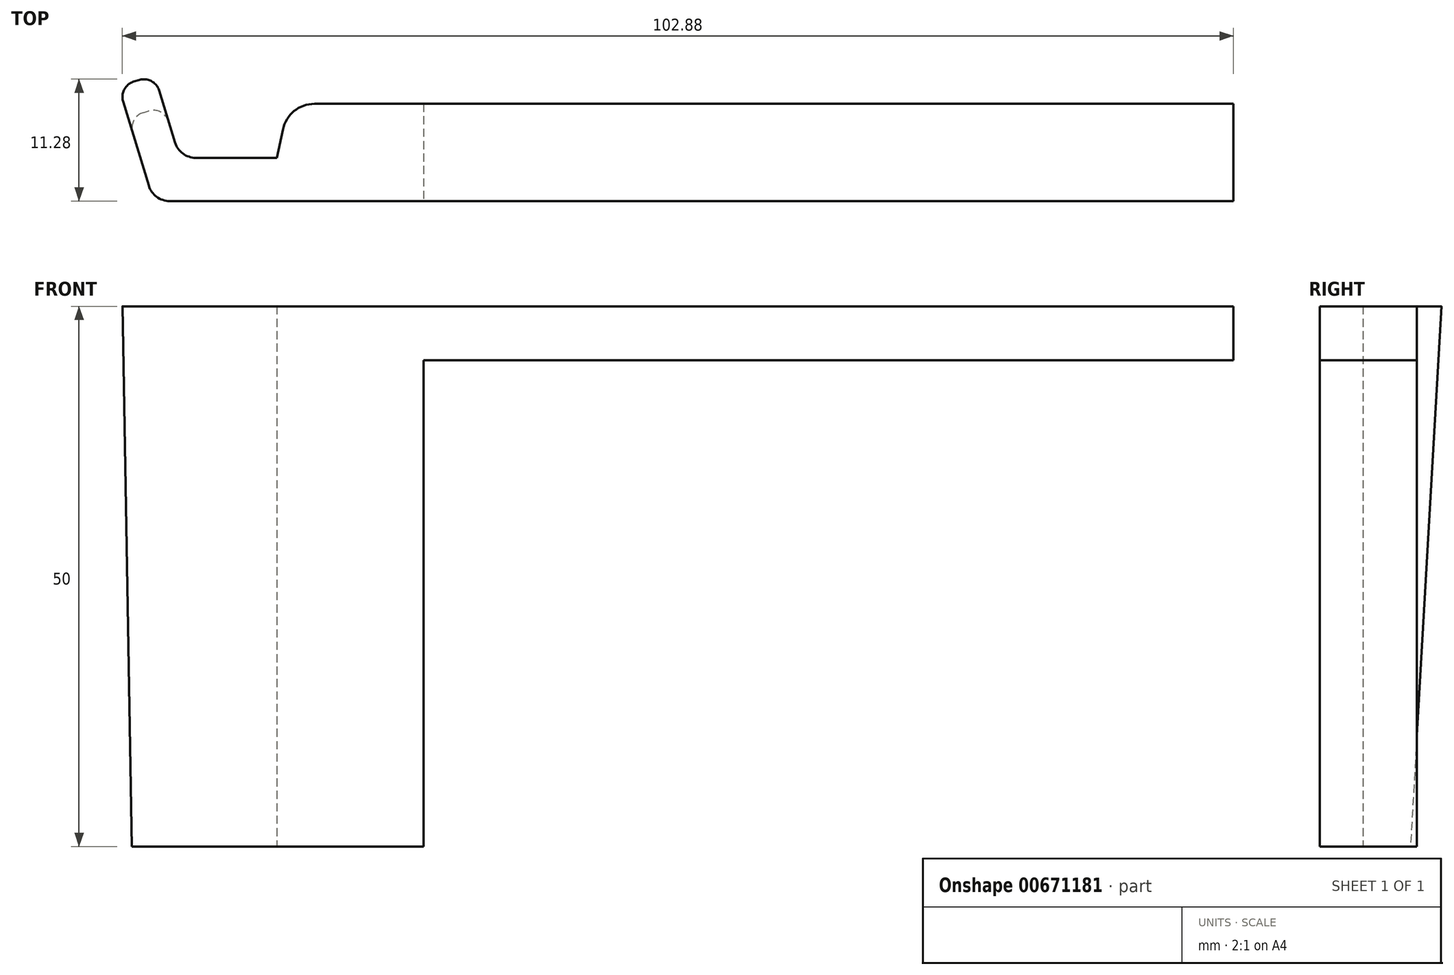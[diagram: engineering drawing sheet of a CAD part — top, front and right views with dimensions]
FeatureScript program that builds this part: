
annotation { "Feature Type Name" : "Feature", "Feature Type Description" : "" }
export const myFeature = defineFeature(function(context is Context, id is Id, definition is map)
    precondition{}
    {
        {
            var Q0;
            Q0=qCreatedBy(makeId("Top.planeOp"),FACE);
            var sketch = newSketch(context, id + "F0", { "sketchPlane" : qUnion([Q0])});
            skLineSegment(sketch, "E0", {"start": v(-7.72, 6.63) * mm, "end": v(-4.47, -4) * mm});
            skLineSegment(sketch, "E1", {"start": v(-4.47, -4) * mm, "end": v(20.53, -4) * mm});
            skLineSegment(sketch, "E2.0", {"start": v(-4.37, 7.65) * mm, "end": v(-2.03, 0) * mm});
            skLineSegment(sketch, "E3", {"start": v(-4.37, 7.65) * mm, "end": v(-7.72, 6.63) * mm});
            skLineSegment(sketch, "E4", {"start": v(6.97, 0) * mm, "end": v(-2.03, 0) * mm});
            skLineSegment(sketch, "E5", {"start": v(20.53, 5) * mm, "end": v(20.53, -4) * mm});
            skLineSegment(sketch, "E6", {"start": v(6.97, 0) * mm, "end": v(8, 5) * mm});
            skLineSegment(sketch, "E7", {"start": v(8, 5) * mm, "end": v(20.53, 5) * mm});
            skPoint(sketch, "E8.orphan", {"position": v(20.53, 0) * mm});
            skPoint(sketch, "E9.orphan", {"position": v(9.05, 10) * mm});
            skSolve(sketch);
        }
        {
            var Q0;
            Q0=qSketchRegion(id+"F0",true);
            extrude(context, id + "F1", {"entities" : qUnion([Q0]), "depth" : 50 * mm, "offsetDistance" : 25 * mm});
        }
        {
            var Q0;
            Q0=makeQuery(id+"F1.opExtrude","CAP_EDGE",EDGE,{"disambiguationData":[OSD([sQuery(id+"F0.wireOp",EDGE,"E3")])],"isStart":true});
            chamfer(context, id + "F2", {"entities" : qUnion([Q0]), "chamferType" : ChamferType.TWO_OFFSETS, "width1" : 50 * mm, "oppositeDirection" : false, "width2" : 3 * mm, "tangentPropagation" : true});
        }
        {
            var Q0;
            Q0=makeQuery(id+"F2.opChamfer","BLEND_EDGE",EDGE,{"blendedFrom":[makeQuery(id+"F1.opExtrude","CAP_EDGE",EDGE,{"disambiguationData":[OSD([sQuery(id+"F0.wireOp",EDGE,"E3")])],"isStart":true}),makeQuery(id+"F1.opExtrude","SWEPT_FACE",FACE,{"disambiguationData":[OSD([sQuery(id+"F0.wireOp",EDGE,"E2.0")])]})],"blendedInto":[makeQuery(id+"F1.opExtrude","SWEPT_FACE",FACE,{"disambiguationData":[OSD([sQuery(id+"F0.wireOp",EDGE,"E2.0")])]})]});
            var Q1;
            Q1=makeQuery(id+"F2.opChamfer","BLEND_EDGE",EDGE,{"blendedFrom":[makeQuery(id+"F1.opExtrude","CAP_EDGE",EDGE,{"disambiguationData":[OSD([sQuery(id+"F0.wireOp",EDGE,"E3")])],"isStart":true}),makeQuery(id+"F1.opExtrude","SWEPT_FACE",FACE,{"disambiguationData":[OSD([sQuery(id+"F0.wireOp",EDGE,"E0")])]})],"blendedInto":[makeQuery(id+"F1.opExtrude","SWEPT_FACE",FACE,{"disambiguationData":[OSD([sQuery(id+"F0.wireOp",EDGE,"E0")])]})]});
            fillet(context, id + "F3", {"entities" : qUnion([Q0, Q1]), "radius" : 1.5 * mm, "tangentPropagation" : true, "allowEdgeOverflow" : false});
        }
        {
            var Q0;
            Q0=makeQuery(id+"F1.opExtrude","SWEPT_EDGE",EDGE,{"disambiguationData":[OSD([sQuery(id+"F0.wireOp",EDGE,"E2.0"),sQuery(id+"F0.wireOp",EDGE,"E4")])]});
            fillet(context, id + "F4", {"entities" : qUnion([Q0]), "radius" : 2 * mm, "tangentPropagation" : true, "allowEdgeOverflow" : false});
        }
        {
            var Q0;
            Q0=makeQuery(id+"F1.opExtrude","SWEPT_EDGE",EDGE,{"disambiguationData":[OSD([sQuery(id+"F0.wireOp",EDGE,"E6"),sQuery(id+"F0.wireOp",EDGE,"E7")])]});
            fillet(context, id + "F5", {"entities" : qUnion([Q0]), "radius" : 3 * mm, "tangentPropagation" : true, "allowEdgeOverflow" : false});
        }
        {
            var Q0;
            Q0=makeQuery(id+"F1.opExtrude","SWEPT_FACE",FACE,{"disambiguationData":[OSD([sQuery(id+"F0.wireOp",EDGE,"E5")])]});
            var sketch = newSketch(context, id + "F6", { "sketchPlane" : qUnion([Q0])});
            skLineSegment(sketch, "E10.bottom", {"start": v(5, 50) * mm, "end": v(-4, 50) * mm});
            skLineSegment(sketch, "E10.top", {"start": v(5, 45) * mm, "end": v(-4, 45) * mm});
            skLineSegment(sketch, "E10.left", {"start": v(5, 50) * mm, "end": v(5, 45) * mm});
            skLineSegment(sketch, "E10.right", {"start": v(-4, 50) * mm, "end": v(-4, 45) * mm});
            skSolve(sketch);
        }
        {
            var Q0;
            Q0 = qSketchRegion(id + "F6", true);
            extrude(context, id + "F7", {"entities" : qUnion([Q0]), "operationType" : NewBodyOperationType.ADD, "depth" : 75 * mm, "offsetDistance" : 25 * mm});
        }
        {
            var Q0;
            Q0=makeQuery(id+"F1.opExtrude","SWEPT_EDGE",EDGE,{"disambiguationData":[OSD([sQuery(id+"F0.wireOp",EDGE,"E0"),sQuery(id+"F0.wireOp",EDGE,"E1")])]});
            fillet(context, id + "F8", {"entities" : qUnion([Q0]), "radius" : 2 * mm, "tangentPropagation" : true, "allowEdgeOverflow" : false});
        }
    });
